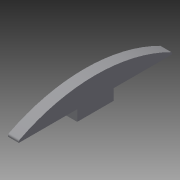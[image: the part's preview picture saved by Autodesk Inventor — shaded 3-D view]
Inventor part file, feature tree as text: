
AUTODESK INVENTOR PART (.ipt)
format: ipt  version: 2013 (Build 170138000, 138)  size: 80,384 bytes
history: native  units: mm
features: extrude x1, sketch x1
ambient origin geometry x8: Origin, YZ Plane, XZ Plane, XY Plane, X Axis, Y Axis, Z Axis, Center Point
bodies: Solid1 (feature_tree)
feature tree (2):
  extrude  "Extrusion1"  Depth=3.0mm
  sketch  "Sketch1"  dims[d3=10.0mm d5=3.0mm d6=3.0mm d7=42.0mm d8=16.0mm d9=0.5mm d10=37.39802mm d12=3.0mm d13=0.0mm]
